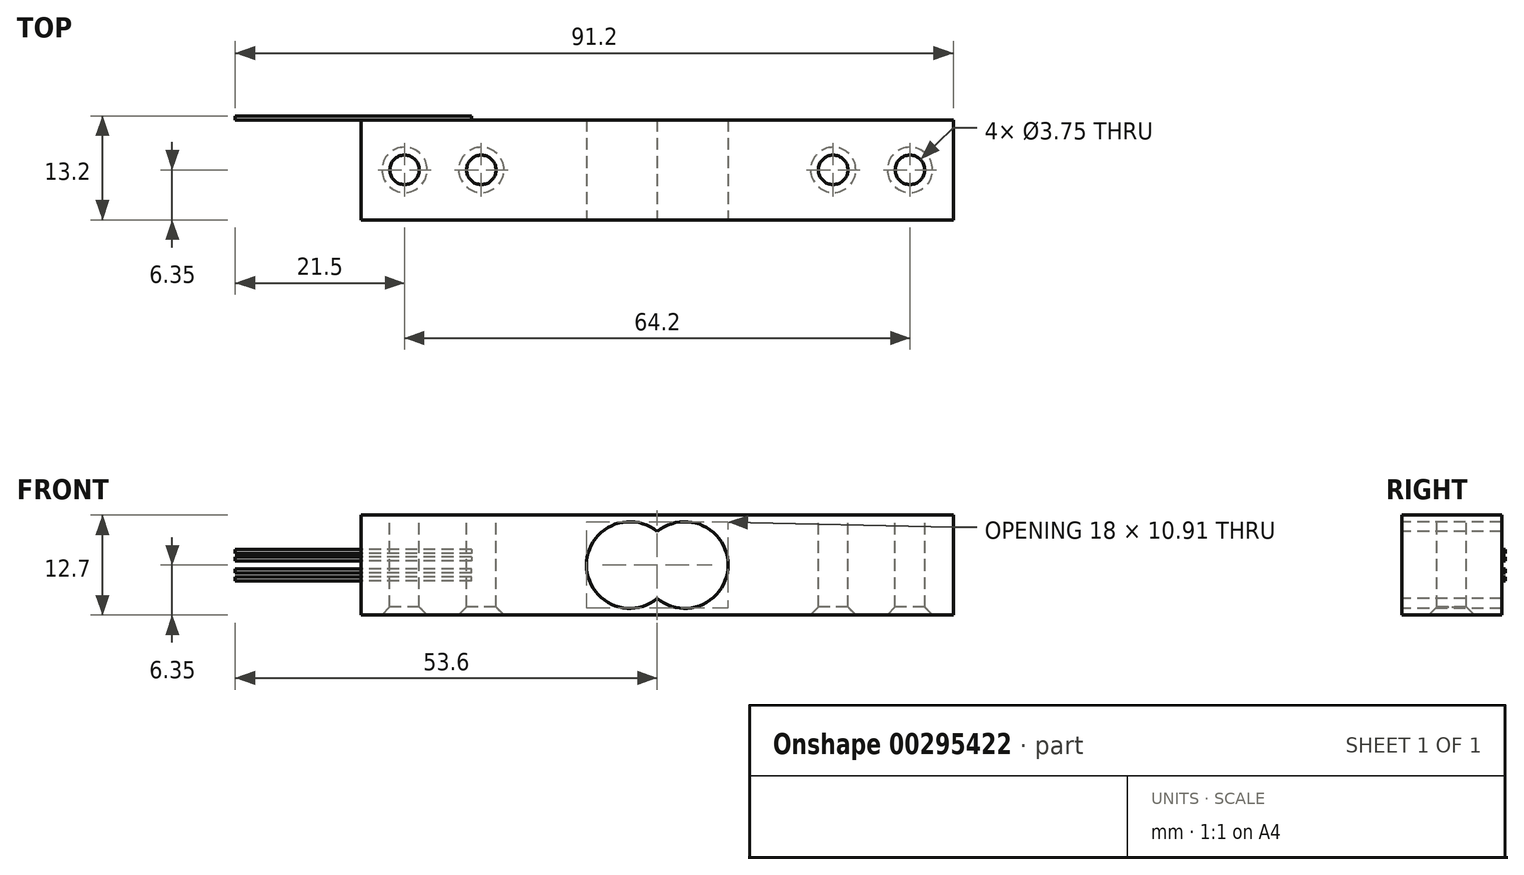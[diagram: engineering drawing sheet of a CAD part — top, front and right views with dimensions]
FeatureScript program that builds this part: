
annotation { "Feature Type Name" : "Feature", "Feature Type Description" : "" }
export const myFeature = defineFeature(function(context is Context, id is Id, definition is map)
    precondition{}
    {
        {
            var Q0;
            Q0=qCreatedBy(makeId("Top.planeOp"),FACE);
            var sketch = newSketch(context, id + "F0", { "sketchPlane" : qUnion([Q0])});
            skLineSegment(sketch, "E0.bottom", {"start": v(37.6, -6.35) * mm, "end": v(-37.6, -6.35) * mm});
            skLineSegment(sketch, "E0.top", {"start": v(37.6, 6.35) * mm, "end": v(-37.6, 6.35) * mm});
            skLineSegment(sketch, "E0.left", {"start": v(37.6, -6.35) * mm, "end": v(37.6, 6.35) * mm});
            skLineSegment(sketch, "E0.right", {"start": v(-37.6, -6.35) * mm, "end": v(-37.6, 6.35) * mm});
            skPoint(sketch, "E0.middle", {"position": v(0, 0) * mm});
            skSolve(sketch);
        }
        {
            var Q0;
            Q0=qSketchRegion(id+"F0",true);
            extrude(context, id + "F1", {"entities" : qUnion([Q0]), "depth" : (12.7 / 2) * mm, "hasSecondDirection" : true, "secondDirectionOppositeDirection" : true, "secondDirectionDepth" : 6.35 * mm});
        }
        {
            var Q0;
            Q0=makeQuery(id+"F1.opExtrude","SWEPT_FACE",FACE,{"disambiguationData":[OSD([sQuery(id+"F0.wireOp",EDGE,"E0.bottom")])]});
            var sketch = newSketch(context, id + "F2", { "sketchPlane" : qUnion([Q0])});
            skLineSegment(sketch, "E1", {"start": v(0, 22.65) * mm, "end": v(0, -18.02) * mm, "construction": true});
            skPoint(sketch, "E1.endSnap0", {"position": v(0, -6.35) * mm});
            skLineSegment(sketch, "E2", {"start": v(-24.04, 0) * mm, "end": v(29.61, 0) * mm, "construction": true});
            skArc(sketch, "E3", {"start": v(0, -4.24) * mm, "mid": v(9, 0) * mm, "end": v(0, 4.24) * mm});
            skLineSegment(sketch, "E4", {"start": v(9, 14.04) * mm, "end": v(9, -17.62) * mm, "construction": true});
            skArc(sketch, "E5.MirrorCS", {"start": v(0, -4.24) * mm, "mid": v(-9, 0) * mm, "end": v(0, 4.24) * mm});
            skSolve(sketch);
        }
        {
            var Q0;
            Q0=qSketchRegion(id+"F2",true);
            extrude(context, id + "F3", {"entities" : qUnion([Q0]), "operationType" : NewBodyOperationType.REMOVE, "oppositeDirection" : true, "depth" : 25 * mm});
        }
        {
            var Q0;
            Q0=makeQuery(id+"F1.opExtrude","SWEPT_FACE",FACE,{"disambiguationData":[OSD([sQuery(id+"F0.wireOp",EDGE,"E0.top")])]});
            var sketch = newSketch(context, id + "F4", { "sketchPlane" : qUnion([Q0])});
            skLineSegment(sketch, "E6", {"start": v(23.6, 18.33) * mm, "end": v(23.6, -21.01) * mm, "construction": true});
            skLineSegment(sketch, "E7.bottom", {"start": v(23.6, 2) * mm, "end": v(53.6, 2) * mm});
            skLineSegment(sketch, "E7.top", {"start": v(23.6, 1.5) * mm, "end": v(53.6, 1.5) * mm});
            skLineSegment(sketch, "E7.left", {"start": v(23.6, 2) * mm, "end": v(23.6, 1.5) * mm});
            skLineSegment(sketch, "E7.right", {"start": v(53.6, 2) * mm, "end": v(53.6, 1.5) * mm});
            skLineSegment(sketch, "E8.0.1.0", {"start": v(23.6, 0.5) * mm, "end": v(53.6, 0.5) * mm});
            skLineSegment(sketch, "E8.0.1.1", {"start": v(23.6, 1) * mm, "end": v(53.6, 1) * mm});
            skLineSegment(sketch, "E8.0.1.2", {"start": v(53.6, 1) * mm, "end": v(53.6, 0.5) * mm});
            skLineSegment(sketch, "E8.0.1.3", {"start": v(23.6, 1) * mm, "end": v(23.6, 0.5) * mm});
            skLineSegment(sketch, "E8.direction1", {"start": v(23.6, 1.5) * mm, "end": v(48.6, 1.5) * mm, "construction": true});
            skLineSegment(sketch, "E8.direction2", {"start": v(23.6, 1.5) * mm, "end": v(23.6, 0.5) * mm, "construction": true});
            skLineSegment(sketch, "E9.MirrorCS", {"start": v(23.6, -1.5) * mm, "end": v(48.6, -1.5) * mm, "construction": true});
            skLineSegment(sketch, "E10.MirrorCS", {"start": v(23.6, -1.5) * mm, "end": v(23.6, -0.5) * mm, "construction": true});
            skLineSegment(sketch, "E11.MirrorCS", {"start": v(23.6, -1) * mm, "end": v(23.6, -0.5) * mm});
            skLineSegment(sketch, "E12.MirrorCS", {"start": v(53.6, -1) * mm, "end": v(53.6, -0.5) * mm});
            skLineSegment(sketch, "E13.MirrorCS", {"start": v(23.6, -2) * mm, "end": v(23.6, -1.5) * mm});
            skLineSegment(sketch, "E14.MirrorCS", {"start": v(53.6, -2) * mm, "end": v(53.6, -1.5) * mm});
            skLineSegment(sketch, "E15.MirrorCS", {"start": v(23.6, -0.5) * mm, "end": v(53.6, -0.5) * mm});
            skLineSegment(sketch, "E16.MirrorCS", {"start": v(23.6, -1) * mm, "end": v(53.6, -1) * mm});
            skLineSegment(sketch, "E17.MirrorCS", {"start": v(23.6, -2) * mm, "end": v(53.6, -2) * mm});
            skLineSegment(sketch, "E18.MirrorCS", {"start": v(23.6, -1.5) * mm, "end": v(53.6, -1.5) * mm});
            skSolve(sketch);
        }
        {
            var Q0;
            Q0=qSketchRegion(id+"F4",true);
            extrude(context, id + "F5", {"entities" : qUnion([Q0]), "operationType" : NewBodyOperationType.ADD, "depth" : 0.5 * mm});
        }
        {
            var Q0;
            Q0=makeQuery(id+"F1.opExtrude","CAP_FACE",FACE,{"disambiguationData":[OSD([sQuery(id+"F0.wireOp",EDGE,"E0.bottom"),sQuery(id+"F0.wireOp",EDGE,"E0.top"),sQuery(id+"F0.wireOp",EDGE,"E0.left"),sQuery(id+"F0.wireOp",EDGE,"E0.right")])],"isStart":false});
            var sketch = newSketch(context, id + "F6", { "sketchPlane" : qUnion([Q0])});
            skCircle(sketch, "E19", {"center": v(32.1, 0) * mm, "radius": 1.88 * mm});
            skCircle(sketch, "E20", {"center": v(22.35, 0) * mm, "radius": 1.88 * mm});
            skCircle(sketch, "E21.MirrorC", {"center": v(-22.35, 0) * mm, "radius": 1.88 * mm});
            skCircle(sketch, "E22.MirrorC", {"center": v(-32.1, 0) * mm, "radius": 1.88 * mm});
            skSolve(sketch);
        }
        {
            var Q0;
            Q0=qSketchRegion(id+"F6",true);
            extrude(context, id + "F7", {"entities" : qUnion([Q0]), "operationType" : NewBodyOperationType.REMOVE, "oppositeDirection" : true, "depth" : 25 * mm});
        }
        {
            var Q0;
            Q0=makeQuery(id+"F7.boolean.opBoolean","COPY",EDGE,{"derivedFrom":makeQuery(id+"F7.opExtrude","CAP_EDGE",EDGE,{"disambiguationData":[OSD([sQuery(id+"F6.wireOp",EDGE,"E19")])],"isStart":true})});
            var Q1;
            Q1=makeQuery(id+"F7.boolean.opBoolean","COPY",EDGE,{"derivedFrom":makeQuery(id+"F7.opExtrude","CAP_EDGE",EDGE,{"disambiguationData":[OSD([sQuery(id+"F6.wireOp",EDGE,"E20")])],"isStart":true})});
            var Q2;
            Q2=makeQuery(id+"F7.boolean.opBoolean","COPY",EDGE,{"derivedFrom":makeQuery(id+"F7.opExtrude","CAP_EDGE",EDGE,{"disambiguationData":[OSD([sQuery(id+"F6.wireOp",EDGE,"E21.MirrorC")])],"isStart":true})});
            var Q3;
            Q3=makeQuery(id+"F7.boolean.opBoolean","COPY",EDGE,{"derivedFrom":makeQuery(id+"F7.opExtrude","CAP_EDGE",EDGE,{"disambiguationData":[OSD([sQuery(id+"F6.wireOp",EDGE,"E22.MirrorC")])],"isStart":true})});
            var Q4;
            Q4=makeQuery(id+"F7.boolean.opBoolean","INTERSECT",EDGE,{"derivedFrom":[makeQuery(id+"F1.opExtrude","CAP_FACE",FACE,{"disambiguationData":[OSD([sQuery(id+"F0.wireOp",EDGE,"E0.bottom"),sQuery(id+"F0.wireOp",EDGE,"E0.top"),sQuery(id+"F0.wireOp",EDGE,"E0.left"),sQuery(id+"F0.wireOp",EDGE,"E0.right")])],"isStart":true}),makeQuery(id+"F7.opExtrude","SWEPT_FACE",FACE,{"disambiguationData":[OSD([sQuery(id+"F6.wireOp",EDGE,"E22.MirrorC")])]})]});
            var Q5;
            Q5=makeQuery(id+"F7.boolean.opBoolean","INTERSECT",EDGE,{"derivedFrom":[makeQuery(id+"F1.opExtrude","CAP_FACE",FACE,{"disambiguationData":[OSD([sQuery(id+"F0.wireOp",EDGE,"E0.bottom"),sQuery(id+"F0.wireOp",EDGE,"E0.top"),sQuery(id+"F0.wireOp",EDGE,"E0.left"),sQuery(id+"F0.wireOp",EDGE,"E0.right")])],"isStart":true}),makeQuery(id+"F7.opExtrude","SWEPT_FACE",FACE,{"disambiguationData":[OSD([sQuery(id+"F6.wireOp",EDGE,"E21.MirrorC")])]})]});
            var Q6;
            Q6=makeQuery(id+"F7.boolean.opBoolean","INTERSECT",EDGE,{"derivedFrom":[makeQuery(id+"F1.opExtrude","CAP_FACE",FACE,{"disambiguationData":[OSD([sQuery(id+"F0.wireOp",EDGE,"E0.bottom"),sQuery(id+"F0.wireOp",EDGE,"E0.top"),sQuery(id+"F0.wireOp",EDGE,"E0.left"),sQuery(id+"F0.wireOp",EDGE,"E0.right")])],"isStart":true}),makeQuery(id+"F7.opExtrude","SWEPT_FACE",FACE,{"disambiguationData":[OSD([sQuery(id+"F6.wireOp",EDGE,"E20")])]})]});
            var Q7;
            Q7=makeQuery(id+"F7.boolean.opBoolean","INTERSECT",EDGE,{"derivedFrom":[makeQuery(id+"F1.opExtrude","CAP_FACE",FACE,{"disambiguationData":[OSD([sQuery(id+"F0.wireOp",EDGE,"E0.bottom"),sQuery(id+"F0.wireOp",EDGE,"E0.top"),sQuery(id+"F0.wireOp",EDGE,"E0.left"),sQuery(id+"F0.wireOp",EDGE,"E0.right")])],"isStart":true}),makeQuery(id+"F7.opExtrude","SWEPT_FACE",FACE,{"disambiguationData":[OSD([sQuery(id+"F6.wireOp",EDGE,"E19")])]})]});
            chamfer(context, id + "F8", {"entities" : qUnion([Q0, Q1, Q2, Q3, Q4, Q5, Q6, Q7]), "width" : 1 * mm, "tangentPropagation" : true});
        }
    });
